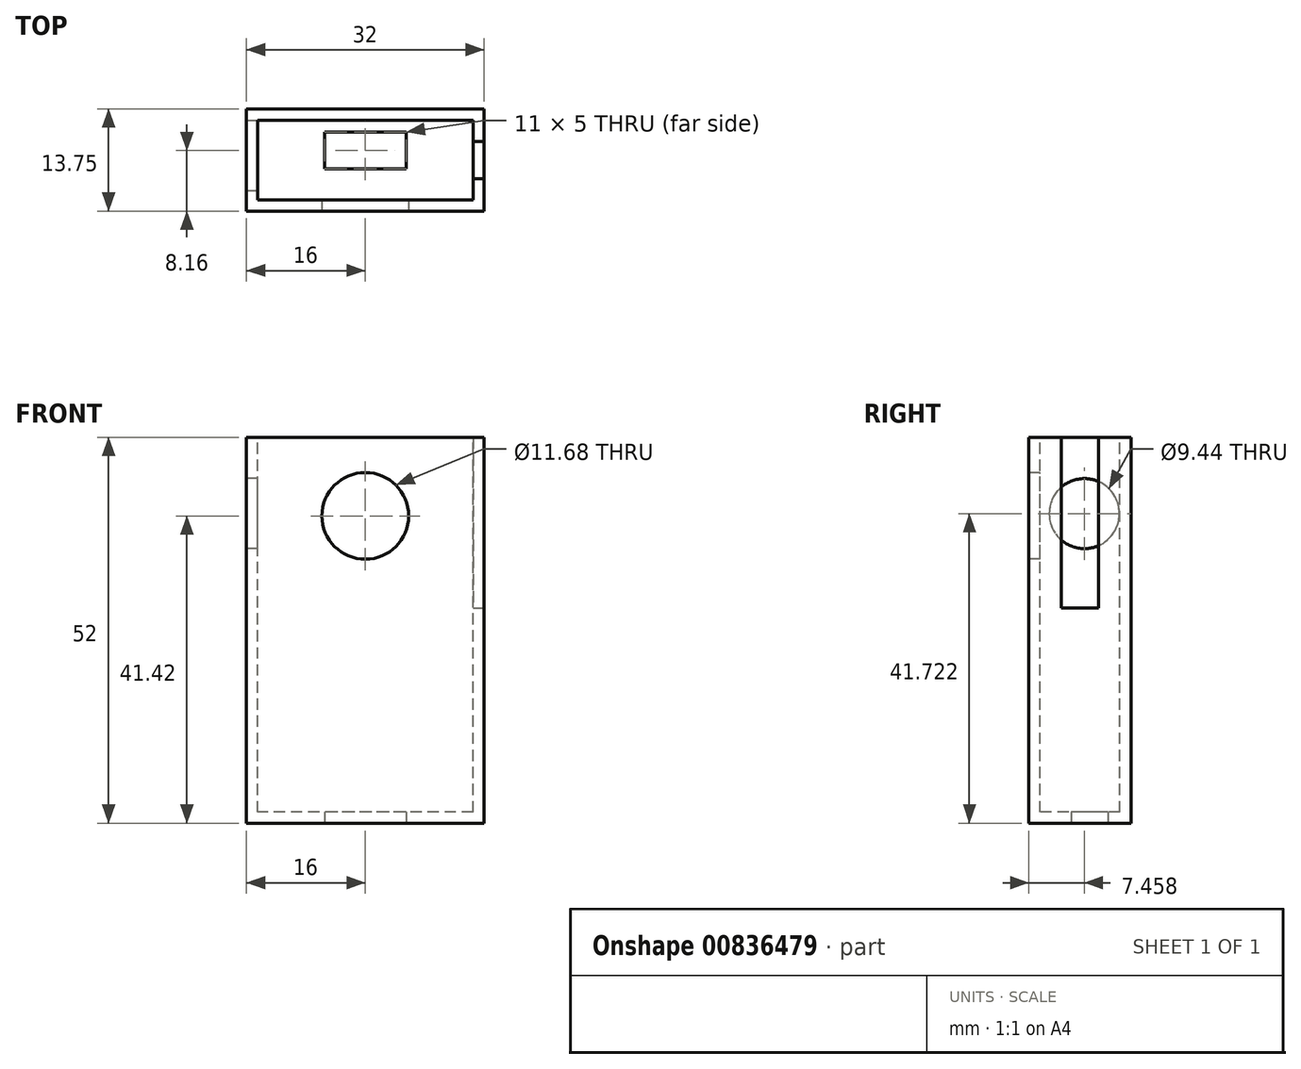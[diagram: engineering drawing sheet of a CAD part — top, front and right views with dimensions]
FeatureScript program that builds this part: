
annotation { "Feature Type Name" : "Feature", "Feature Type Description" : "" }
export const myFeature = defineFeature(function(context is Context, id is Id, definition is map)
    precondition{}
    {
        {
            var Q0;
            Q0=qCreatedBy(makeId("Front.planeOp"),FACE);
            var sketch = newSketch(context, id + "F0", { "sketchPlane" : qUnion([Q0])});
            skLineSegment(sketch, "E0.bottom", {"start": v(16, -26) * mm, "end": v(-16, -26) * mm});
            skLineSegment(sketch, "E0.top", {"start": v(16, 26) * mm, "end": v(-16, 26) * mm});
            skLineSegment(sketch, "E0.left", {"start": v(16, -26) * mm, "end": v(16, 26) * mm});
            skLineSegment(sketch, "E0.right", {"start": v(-16, -26) * mm, "end": v(-16, 26) * mm});
            skPoint(sketch, "E0.middle", {"position": v(0, 0) * mm});
            skSolve(sketch);
        }
        {
            var Q0;
            Q0=makeQuery(id+"F0.imprint","IMPRINT",FACE,{"disambiguationData":[TD([[makeQuery(id+"F0.imprint","IMPRINT",EDGE,{"derivedFrom":sQuery(id+"F0.wireOp",EDGE,"E0.bottom")}),-1.0]])]});
            extrude(context, id + "F1", {"entities" : qUnion([Q0]), "oppositeDirection" : true, "depth" : 13.75 * mm, "offsetDistance" : 25 * mm});
        }
        {
            var Q0;
            Q0=makeQuery(id+"F1.opExtrude","SWEPT_FACE",FACE,{"disambiguationData":[OSD([sQuery(id+"F0.wireOp",EDGE,"E0.top")])]});
            shell(context, id + "F2", {"entities" : qUnion([Q0]), "thickness" : 1.5 * mm});
        }
        {
            var Q0;
            Q0=qCreatedBy(makeId("Front.planeOp"),FACE);
            var sketch = newSketch(context, id + "F3", { "sketchPlane" : qUnion([Q0])});
            skCircle(sketch, "E1", {"center": v(0, 15.42) * mm, "radius": 5.84 * mm});
            skSolve(sketch);
        }
        {
            var Q0;
            Q0 = qSketchRegion(id + "F3", true);
            var Q1;
            Q1=sQuery(id+"F3.wireOp",EDGE,"E1");
            extrude(context, id + "F4", {"entities" : qUnion([Q0]), "operationType" : NewBodyOperationType.REMOVE, "surfaceEntities" : qUnion([Q1]), "oppositeDirection" : true, "depth" : 1.5 * mm, "offsetDistance" : 25 * mm});
        }
        {
            var Q0;
            Q0=makeQuery(id+"F1.opExtrude","SWEPT_FACE",FACE,{"disambiguationData":[OSD([sQuery(id+"F0.wireOp",EDGE,"E0.right")])]});
            var sketch = newSketch(context, id + "F5", { "sketchPlane" : qUnion([Q0])});
            skCircle(sketch, "E2", {"center": v(-7.46, 15.72) * mm, "radius": 4.72 * mm});
            skSolve(sketch);
        }
        {
            var Q0;
            Q0=makeQuery(id+"F5.imprint","IMPRINT",FACE,{"disambiguationData":[TD([[makeQuery(id+"F5.imprint","IMPRINT",EDGE,{"derivedFrom":sQuery(id+"F5.wireOp",EDGE,"E2")}),1.0]])]});
            extrude(context, id + "F6", {"entities" : qUnion([Q0]), "operationType" : NewBodyOperationType.REMOVE, "oppositeDirection" : true, "depth" : 3 * mm, "offsetDistance" : 25 * mm});
        }
        {
            var Q0;
            Q0=makeQuery(id+"F1.opExtrude","SWEPT_FACE",FACE,{"disambiguationData":[OSD([sQuery(id+"F0.wireOp",EDGE,"E0.left")])]});
            var sketch = newSketch(context, id + "F7", { "sketchPlane" : qUnion([Q0])});
            skLineSegment(sketch, "E3.bottom", {"start": v(4.38, 26) * mm, "end": v(9.38, 26) * mm});
            skLineSegment(sketch, "E3.top", {"start": v(4.38, 3) * mm, "end": v(9.38, 3) * mm});
            skLineSegment(sketch, "E3.left", {"start": v(4.38, 26) * mm, "end": v(4.38, 3) * mm});
            skLineSegment(sketch, "E3.right", {"start": v(9.38, 26) * mm, "end": v(9.38, 3) * mm});
            skSolve(sketch);
        }
        {
            var Q0;
            Q0=makeQuery(id+"F7.imprint","IMPRINT",FACE,{"disambiguationData":[TD([[makeQuery(id+"F7.imprint","IMPRINT",EDGE,{"derivedFrom":sQuery(id+"F7.wireOp",EDGE,"E3.bottom")}),1.0]])]});
            var Q1;
            Q1=sQuery(id+"F7.wireOp",EDGE,"E3.top");
            extrude(context, id + "F8", {"entities" : qUnion([Q0]), "operationType" : NewBodyOperationType.REMOVE, "surfaceEntities" : qUnion([Q1]), "oppositeDirection" : true, "depth" : 2 * mm, "offsetDistance" : 25 * mm});
        }
        {
            var Q0;
            Q0=makeQuery(id+"F1.opExtrude","SWEPT_FACE",FACE,{"disambiguationData":[OSD([sQuery(id+"F0.wireOp",EDGE,"E0.bottom")])]});
            var sketch = newSketch(context, id + "F9", { "sketchPlane" : qUnion([Q0])});
            skLineSegment(sketch, "E4.bottom", {"start": v(-5.5, -5.66) * mm, "end": v(5.5, -5.66) * mm});
            skLineSegment(sketch, "E4.top", {"start": v(-5.5, -10.66) * mm, "end": v(5.5, -10.66) * mm});
            skLineSegment(sketch, "E4.left", {"start": v(-5.5, -5.66) * mm, "end": v(-5.5, -10.66) * mm});
            skLineSegment(sketch, "E4.right", {"start": v(5.5, -5.66) * mm, "end": v(5.5, -10.66) * mm});
            skSolve(sketch);
        }
        {
            var Q0;
            Q0=makeQuery(id+"F9.imprint","IMPRINT",FACE,{"disambiguationData":[TD([[makeQuery(id+"F9.imprint","IMPRINT",EDGE,{"derivedFrom":sQuery(id+"F9.wireOp",EDGE,"E4.bottom")}),-1.0]])]});
            extrude(context, id + "F10", {"entities" : qUnion([Q0]), "operationType" : NewBodyOperationType.REMOVE, "oppositeDirection" : true, "depth" : 2 * mm, "offsetDistance" : 25 * mm});
        }
    });
